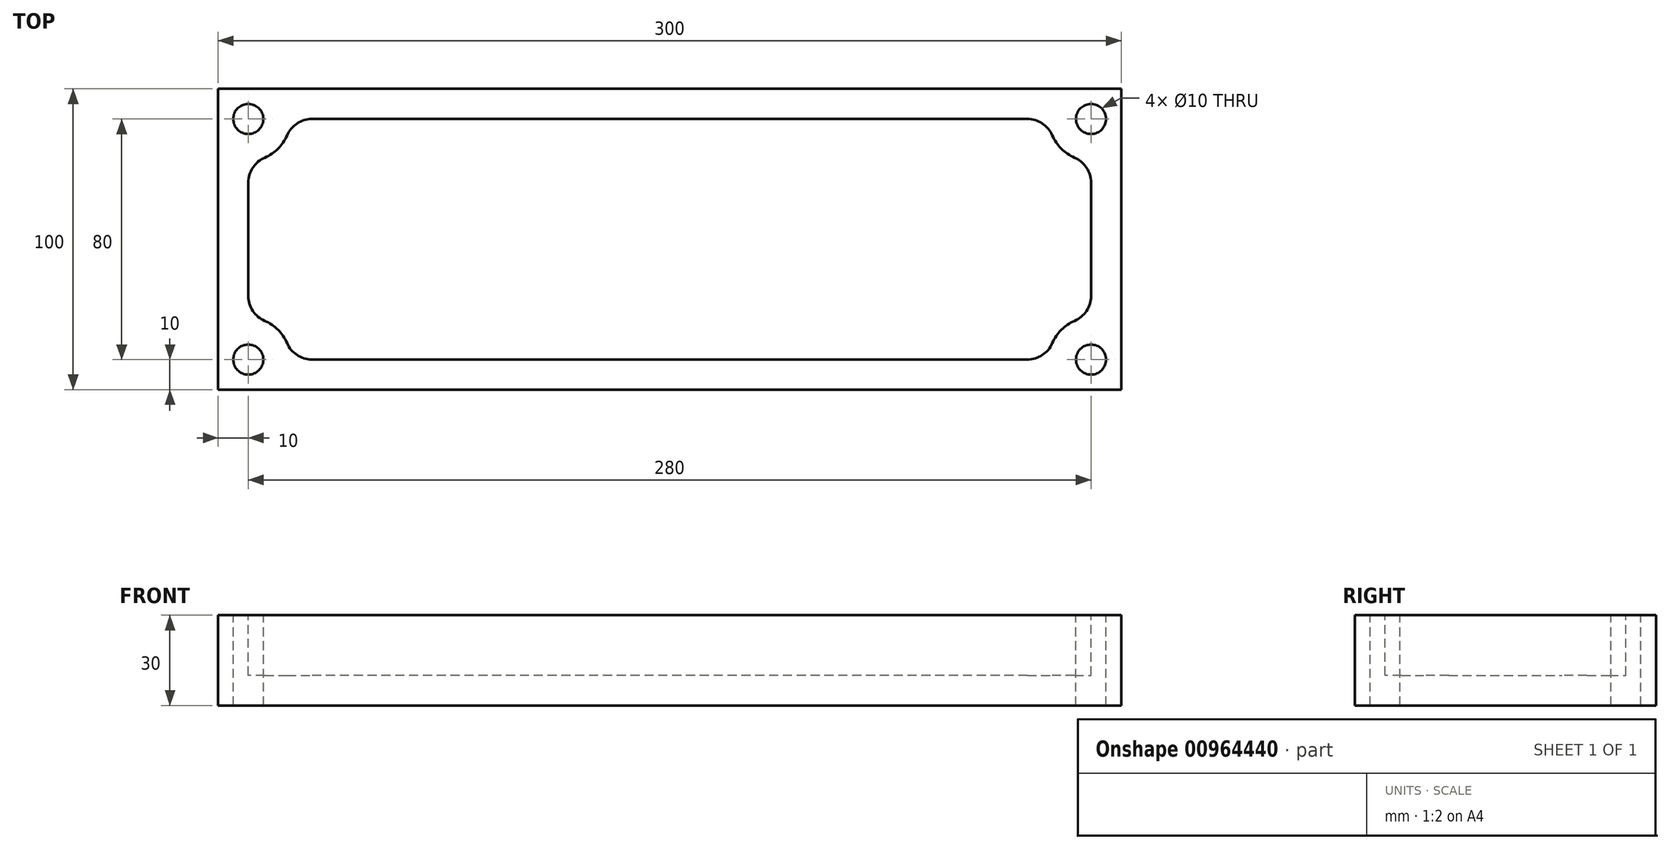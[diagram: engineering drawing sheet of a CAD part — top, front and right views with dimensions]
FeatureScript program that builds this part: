
annotation { "Feature Type Name" : "Feature", "Feature Type Description" : "" }
export const myFeature = defineFeature(function(context is Context, id is Id, definition is map)
    precondition{}
    {
        {
            var Q0;
            Q0=qCreatedBy(makeId("Top.planeOp"),FACE);
            var sketch = newSketch(context, id + "F0", { "sketchPlane" : qUnion([Q0])});
            skLineSegment(sketch, "E0.bottom", {"start": v(0, 0) * mm, "end": v(300, 0) * mm});
            skLineSegment(sketch, "E0.top", {"start": v(0, 100) * mm, "end": v(300, 100) * mm});
            skLineSegment(sketch, "E0.left", {"start": v(0, 0) * mm, "end": v(0, 100) * mm});
            skLineSegment(sketch, "E0.right", {"start": v(300, 0) * mm, "end": v(300, 100) * mm});
            skSolve(sketch);
        }
        {
            var Q0;
            Q0=makeQuery(id+"F0.imprint","IMPRINT",FACE,{"disambiguationData":[TD([[makeQuery(id+"F0.imprint","IMPRINT",EDGE,{"derivedFrom":sQuery(id+"F0.wireOp",EDGE,"E0.bottom")}),1.0]])]});
            extrude(context, id + "F1", {"entities" : qUnion([Q0]), "depth" : 30 * mm, "offsetDistance" : 25 * mm});
        }
        {
            var Q0;
            Q0=makeQuery(id+"F1.opExtrude","CAP_FACE",FACE,{"disambiguationData":[OSD([sQuery(id+"F0.wireOp",EDGE,"E0.bottom"),sQuery(id+"F0.wireOp",EDGE,"E0.top"),sQuery(id+"F0.wireOp",EDGE,"E0.left"),sQuery(id+"F0.wireOp",EDGE,"E0.right")])],"isStart":false});
            var sketch = newSketch(context, id + "F2", { "sketchPlane" : qUnion([Q0])});
            skLineSegment(sketch, "E1", {"start": v(150, 90) * mm, "end": v(268.83, 90) * mm});
            skArc(sketch, "E2", {"start": v(277.12, 84.52) * mm, "mid": v(273.8, 88.5) * mm, "end": v(268.83, 90) * mm});
            skArc(sketch, "E3", {"start": v(277.12, 84.52) * mm, "mid": v(280.1, 80.1) * mm, "end": v(284.52, 77.12) * mm});
            skArc(sketch, "E4", {"start": v(290, 68.83) * mm, "mid": v(288.5, 73.8) * mm, "end": v(284.52, 77.12) * mm});
            skLineSegment(sketch, "E5", {"start": v(290, 50) * mm, "end": v(290, 68.83) * mm});
            skLineSegment(sketch, "E6", {"start": v(0, 50) * mm, "end": v(300, 50) * mm, "construction": true});
            skLineSegment(sketch, "E7", {"start": v(150, 100) * mm, "end": v(150, 0) * mm, "construction": true});
            skLineSegment(sketch, "E8", {"start": v(290, 90) * mm, "end": v(250.4, 90) * mm, "construction": true});
            skLineSegment(sketch, "E9", {"start": v(290, 68.83) * mm, "end": v(290, 90) * mm, "construction": true});
            skArc(sketch, "E10.MirrorCS", {"start": v(10, 68.83) * mm, "mid": v(11.5, 73.8) * mm, "end": v(15.48, 77.12) * mm});
            skArc(sketch, "E11.MirrorCS", {"start": v(22.88, 84.52) * mm, "mid": v(19.9, 80.1) * mm, "end": v(15.48, 77.12) * mm});
            skArc(sketch, "E12.MirrorCS", {"start": v(22.88, 84.52) * mm, "mid": v(26.2, 88.5) * mm, "end": v(31.17, 90) * mm});
            skLineSegment(sketch, "E13.MirrorCS", {"start": v(10, 68.83) * mm, "end": v(10, 90) * mm, "construction": true});
            skLineSegment(sketch, "E14.MirrorCS", {"start": v(10, 90) * mm, "end": v(49.6, 90) * mm, "construction": true});
            skLineSegment(sketch, "E15.MirrorCS", {"start": v(150, 90) * mm, "end": v(31.17, 90) * mm});
            skLineSegment(sketch, "E16.MirrorCS", {"start": v(10, 50) * mm, "end": v(10, 68.83) * mm});
            skArc(sketch, "E17.MirrorCS", {"start": v(10, 31.17) * mm, "mid": v(11.5, 26.2) * mm, "end": v(15.48, 22.88) * mm});
            skArc(sketch, "E18.MirrorCS", {"start": v(22.88, 15.48) * mm, "mid": v(26.2, 11.5) * mm, "end": v(31.17, 10) * mm});
            skLineSegment(sketch, "E19.MirrorCS", {"start": v(10, 10) * mm, "end": v(49.6, 10) * mm, "construction": true});
            skArc(sketch, "E20.MirrorCS", {"start": v(22.88, 15.48) * mm, "mid": v(19.9, 19.9) * mm, "end": v(15.48, 22.88) * mm});
            skLineSegment(sketch, "E21.MirrorCS", {"start": v(10, 31.17) * mm, "end": v(10, 10) * mm, "construction": true});
            skLineSegment(sketch, "E22.MirrorCS", {"start": v(10, 50) * mm, "end": v(10, 31.17) * mm});
            skLineSegment(sketch, "E23.MirrorCS", {"start": v(150, 10) * mm, "end": v(31.17, 10) * mm});
            skArc(sketch, "E24.MirrorCS", {"start": v(277.12, 15.48) * mm, "mid": v(280.1, 19.9) * mm, "end": v(284.52, 22.88) * mm});
            skLineSegment(sketch, "E25.MirrorCS", {"start": v(290, 50) * mm, "end": v(290, 31.17) * mm});
            skArc(sketch, "E26.MirrorCS", {"start": v(277.12, 15.48) * mm, "mid": v(273.8, 11.5) * mm, "end": v(268.83, 10) * mm});
            skArc(sketch, "E27.MirrorCS", {"start": v(290, 31.17) * mm, "mid": v(288.5, 26.2) * mm, "end": v(284.52, 22.88) * mm});
            skLineSegment(sketch, "E28.MirrorCS", {"start": v(290, 10) * mm, "end": v(250.4, 10) * mm, "construction": true});
            skLineSegment(sketch, "E29.MirrorCS", {"start": v(150, 10) * mm, "end": v(268.83, 10) * mm});
            skLineSegment(sketch, "E30.MirrorCS", {"start": v(290, 31.17) * mm, "end": v(290, 10) * mm, "construction": true});
            skSolve(sketch);
        }
        {
            var Q0;
            Q0=makeQuery(id+"F2.imprint","IMPRINT",FACE,{"disambiguationData":[TD([[makeQuery(id+"F2.imprint","IMPRINT",EDGE,{"derivedFrom":sQuery(id+"F2.wireOp",EDGE,"E1")}),-1.0]])]});
            extrude(context, id + "F3", {"entities" : qUnion([Q0]), "operationType" : NewBodyOperationType.REMOVE, "oppositeDirection" : true, "depth" : 20 * mm, "offsetDistance" : 25 * mm});
        }
        {
            var Q0;
            Q0=makeQuery(id+"F1.opExtrude","CAP_FACE",FACE,{"disambiguationData":[OSD([sQuery(id+"F0.wireOp",EDGE,"E0.bottom"),sQuery(id+"F0.wireOp",EDGE,"E0.top"),sQuery(id+"F0.wireOp",EDGE,"E0.left"),sQuery(id+"F0.wireOp",EDGE,"E0.right")])],"isStart":false});
            var sketch = newSketch(context, id + "F4", { "sketchPlane" : qUnion([Q0])});
            skCircle(sketch, "E31", {"center": v(290, 90) * mm, "radius": 5 * mm});
            skLineSegment(sketch, "E32", {"start": v(0, 50) * mm, "end": v(300, 50) * mm, "construction": true});
            skLineSegment(sketch, "E33", {"start": v(150, 100) * mm, "end": v(150, 0) * mm, "construction": true});
            skCircle(sketch, "E34.MirrorC", {"center": v(10, 90) * mm, "radius": 5 * mm});
            skCircle(sketch, "E35.MirrorC", {"center": v(10, 10) * mm, "radius": 5 * mm});
            skCircle(sketch, "E36.MirrorC", {"center": v(290, 10) * mm, "radius": 5 * mm});
            skSolve(sketch);
        }
        {
            var Q0;
            Q0 = qSketchRegion(id + "F4", true);
            extrude(context, id + "F5", {"entities" : qUnion([Q0]), "operationType" : NewBodyOperationType.REMOVE, "endBound" : BoundingType.THROUGH_ALL, "oppositeDirection" : true, "depth" : 25 * mm, "offsetDistance" : 25 * mm});
        }
    });
